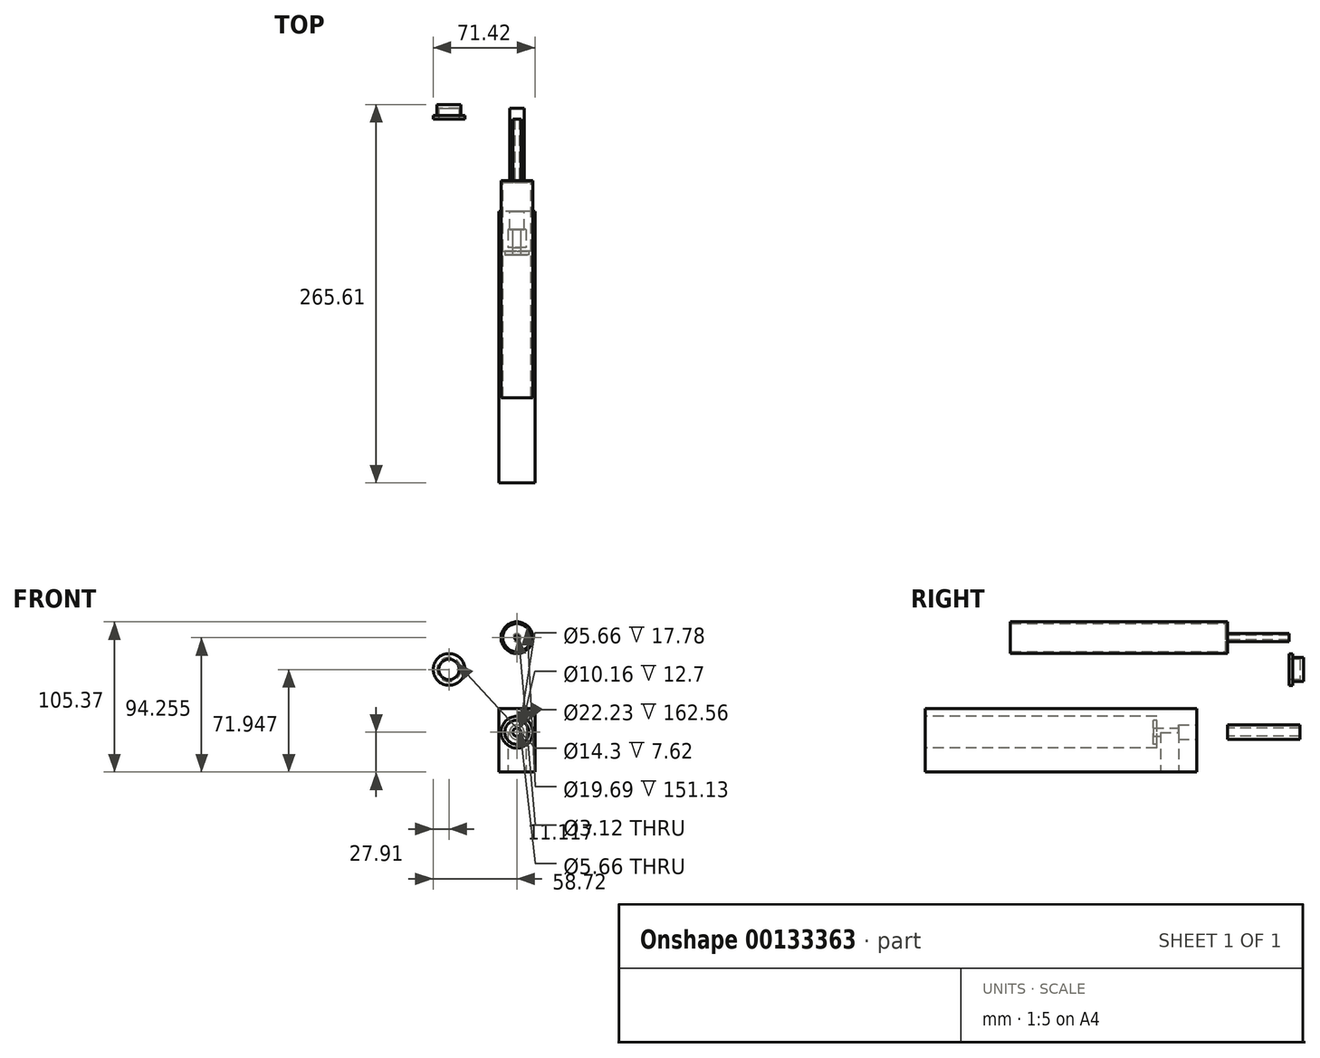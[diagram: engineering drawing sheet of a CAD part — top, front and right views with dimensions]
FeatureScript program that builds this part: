
annotation { "Feature Type Name" : "Feature", "Feature Type Description" : "" }
export const myFeature = defineFeature(function(context is Context, id is Id, definition is map)
    precondition{}
    {
        {
            var Q0;
            Q0=qCreatedBy(makeId("Right.planeOp"),FACE);
            var sketch = newSketch(context, id + "F0", { "sketchPlane" : qUnion([Q0])});
            skLineSegment(sketch, "E0.bottom", {"start": v(0, 0) * mm, "end": v(50.8, 0) * mm});
            skLineSegment(sketch, "E0.top", {"start": v(0, -2.83) * mm, "end": v(50.8, -2.83) * mm});
            skLineSegment(sketch, "E0.left", {"start": v(0, 0) * mm, "end": v(0, -2.83) * mm});
            skLineSegment(sketch, "E0.right", {"start": v(50.8, 0) * mm, "end": v(50.8, -2.83) * mm});
            skLineSegment(sketch, "E1.top", {"start": v(0, -5.08) * mm, "end": v(50.8, -5.08) * mm});
            skLineSegment(sketch, "E1.left", {"start": v(0, 0) * mm, "end": v(0, -5.08) * mm});
            skLineSegment(sketch, "E1.right", {"start": v(50.8, 0) * mm, "end": v(50.8, -5.08) * mm});
            skLineSegment(sketch, "E2.bottom", {"start": v(-21.77, 10.19) * mm, "end": v(-97.97, 10.19) * mm});
            skLineSegment(sketch, "E2.top", {"start": v(-21.77, -27.91) * mm, "end": v(-97.97, -27.91) * mm});
            skLineSegment(sketch, "E2.left", {"start": v(-21.77, 10.19) * mm, "end": v(-21.77, -27.91) * mm});
            skLineSegment(sketch, "E2.right", {"start": v(-97.97, 10.19) * mm, "end": v(-97.97, -27.91) * mm});
            skLineSegment(sketch, "E3.bottom", {"start": v(-97.97, 10.19) * mm, "end": v(-212.27, 10.19) * mm});
            skLineSegment(sketch, "E3.top", {"start": v(-97.97, -27.91) * mm, "end": v(-212.27, -27.91) * mm});
            skLineSegment(sketch, "E3.right", {"start": v(-212.27, 10.19) * mm, "end": v(-212.27, -27.91) * mm});
            skLineSegment(sketch, "E4.bottom", {"start": v(-212.27, 10.19) * mm, "end": v(-21.77, 10.19) * mm});
            skLineSegment(sketch, "E4.top", {"start": v(-212.27, 16.54) * mm, "end": v(-21.77, 16.54) * mm});
            skLineSegment(sketch, "E4.left", {"start": v(-212.27, 10.19) * mm, "end": v(-212.27, 16.54) * mm});
            skLineSegment(sketch, "E4.right", {"start": v(-21.77, 10.19) * mm, "end": v(-21.77, 16.54) * mm});
            skSolve(sketch);
        }
        {
            var Q0;
            {var subQ0=sQuery(id+"F0.wireOp",EDGE,"E0.top");Q0=makeQuery(id+"F0.imprint","IMPRINT",FACE,{"disambiguationData":[TD([[makeQuery(id+"F0.imprint","IMPRINT",EDGE,{"derivedFrom":subQ0}),-1.0]])]});}
            var Q1;
            Q1=sQuery(id+"F0.wireOp",EDGE,"E0.bottom");
            revolve(context, id + "F1", {"entities" : qUnion([Q0]), "axis" : qUnion([Q1]), "revolveType" : RevolveType.FULL});
        }
        {
            var Q0;
            Q0=makeQuery(id+"F0.imprint","IMPRINT",FACE,{"disambiguationData":[TD([[makeQuery(id+"F0.imprint","IMPRINT",EDGE,{"derivedFrom":sQuery(id+"F0.wireOp",EDGE,"E3.top")}),-1.0]])]});
            var Q1;
            Q1=makeQuery(id+"F0.imprint","IMPRINT",FACE,{"disambiguationData":[TD([[makeQuery(id+"F0.imprint","IMPRINT",EDGE,{"derivedFrom":sQuery(id+"F0.wireOp",EDGE,"E4.top")}),-1.0]])]});
            var Q2;
            Q2=makeQuery(id+"F0.imprint","IMPRINT",FACE,{"disambiguationData":[TD([[makeQuery(id+"F0.imprint","IMPRINT",EDGE,{"derivedFrom":sQuery(id+"F0.wireOp",EDGE,"E2.top")}),-1.0]])]});
            extrude(context, id + "F2", {"entities" : qUnion([Q0, Q1, Q2]), "operationType" : NewBodyOperationType.ADD, "endBound" : BoundingType.SYMMETRIC, "depth" : 25.4 * mm});
        }
        {
            var Q0;
            Q0=makeQuery(id+"F2.opExtrude","SWEPT_FACE",FACE,{"disambiguationData":[OSD([sQuery(id+"F0.wireOp",EDGE,"E2.left")])]});
            var sketch = newSketch(context, id + "F3", { "sketchPlane" : qUnion([Q0])});
            skPoint(sketch, "E5", {"position": v(0, -38.2) * mm});
            skPoint(sketch, "E5.positionSnap0", {"position": v(0, -27.91) * mm});
            skCircle(sketch, "E6", {"center": v(0, 0) * mm, "radius": 5.08 * mm});
            skCircle(sketch, "E7", {"center": v(0, 0) * mm, "radius": 2.83 * mm});
            skSolve(sketch);
        }
        {
            var Q0;
            Q0=makeQuery(id+"F3.imprint","IMPRINT",FACE,{"disambiguationData":[TD([[makeQuery(id+"F3.imprint","IMPRINT",EDGE,{"derivedFrom":sQuery(id+"F3.wireOp",EDGE,"E6")}),1.0]])]});
            extrude(context, id + "F4", {"entities" : qUnion([Q0]), "operationType" : NewBodyOperationType.REMOVE, "oppositeDirection" : true, "depth" : 12.7 * mm});
        }
        {
            var Q0;
            Q0=makeQuery(id+"F4.boolean.opBoolean","SPLIT",FACE,{"disambiguationData":[TD([makeQuery(id+"F4.opExtrude","SWEPT_FACE",FACE,{"disambiguationData":[OSD([sQuery(id+"F3.wireOp",EDGE,"E7")])]})])],"derivedFrom":makeQuery(id+"F2.opExtrude","SWEPT_FACE",FACE,{"disambiguationData":[OSD([sQuery(id+"F0.wireOp",EDGE,"E2.left")])]})});
            extrude(context, id + "F5", {"entities" : qUnion([Q0]), "operationType" : NewBodyOperationType.REMOVE, "oppositeDirection" : true, "depth" : 190.5 * mm});
        }
        {
            var Q0;
            Q0=makeQuery(id+"F2.opExtrude","SWEPT_FACE",FACE,{"disambiguationData":[OSD([sQuery(id+"F0.wireOp",EDGE,"E2.top")])]});
            var sketch = newSketch(context, id + "F6", { "sketchPlane" : qUnion([Q0])});
            skPoint(sketch, "E8", {"position": v(0, 34.47) * mm});
            skPoint(sketch, "E8.positionSnap0", {"position": v(0, 21.77) * mm});
            skPoint(sketch, "E9", {"position": v(0, 40.82) * mm});
            skLineSegment(sketch, "E10.bottom", {"start": v(6.35, 34.47) * mm, "end": v(-6.35, 34.47) * mm});
            skLineSegment(sketch, "E10.top", {"start": v(6.35, 47.17) * mm, "end": v(-6.35, 47.17) * mm});
            skLineSegment(sketch, "E10.left", {"start": v(6.35, 34.47) * mm, "end": v(6.35, 47.17) * mm});
            skLineSegment(sketch, "E10.right", {"start": v(-6.35, 34.47) * mm, "end": v(-6.35, 47.17) * mm});
            skSolve(sketch);
        }
        {
            var Q0;
            Q0=makeQuery(id+"F6.imprint","IMPRINT",FACE,{"disambiguationData":[TD([[makeQuery(id+"F6.imprint","IMPRINT",EDGE,{"derivedFrom":sQuery(id+"F6.wireOp",EDGE,"E10.bottom")}),-1.0]])]});
            extrude(context, id + "F7", {"entities" : qUnion([Q0]), "operationType" : NewBodyOperationType.REMOVE, "oppositeDirection" : true, "depth" : 27.8 * mm});
        }
        {
            var Q0;
            Q0=makeQuery(id+"F2.opExtrude","SWEPT_FACE",FACE,{"disambiguationData":[OSD([sQuery(id+"F0.wireOp",EDGE,"E3.right")])]});
            var sketch = newSketch(context, id + "F8", { "sketchPlane" : qUnion([Q0])});
            skCircle(sketch, "E11", {"center": v(0, 0) * mm, "radius": 11.11 * mm});
            skCircle(sketch, "E12", {"center": v(0, 0) * mm, "radius": 8.42 * mm});
            skSolve(sketch);
        }
        {
            var Q0;
            Q0=makeQuery(id+"F8.imprint","IMPRINT",FACE,{"disambiguationData":[TD([[makeQuery(id+"F8.imprint","IMPRINT",EDGE,{"derivedFrom":sQuery(id+"F8.wireOp",EDGE,"E11")}),1.0]])]});
            var Q1;
            Q1=makeQuery(id+"F8.imprint","IMPRINT",FACE,{"disambiguationData":[TD([[makeQuery(id+"F8.imprint","IMPRINT",EDGE,{"derivedFrom":sQuery(id+"F8.wireOp",EDGE,"E12")}),1.0]])]});
            extrude(context, id + "F9", {"entities" : qUnion([Q0, Q1]), "operationType" : NewBodyOperationType.REMOVE, "oppositeDirection" : true, "depth" : 160.02 * mm});
        }
        {
            var Q0;
            Q0=qCreatedBy(makeId("Front.planeOp"),FACE);
            var sketch = newSketch(context, id + "F10", { "sketchPlane" : qUnion([Q0])});
            skCircle(sketch, "E13", {"center": v(0, 25.97) * mm, "radius": 11.11 * mm});
            skCircle(sketch, "E14", {"center": v(0, 25.97) * mm, "radius": 2.83 * mm});
            skSolve(sketch);
        }
        {
            var Q0;
            Q0=makeQuery(id+"F10.imprint","IMPRINT",FACE,{"disambiguationData":[TD([[makeQuery(id+"F10.imprint","IMPRINT",EDGE,{"derivedFrom":sQuery(id+"F10.wireOp",EDGE,"E13")}),1.0]])]});
            var Q1;
            Q1=makeQuery(id+"F10.imprint","IMPRINT",FACE,{"disambiguationData":[TD([[makeQuery(id+"F10.imprint","IMPRINT",EDGE,{"derivedFrom":sQuery(id+"F10.wireOp",EDGE,"E14")}),1.0]])]});
            extrude(context, id + "F11", {"entities" : qUnion([Q0, Q1]), "depth" : 152.4 * mm});
        }
        {
            var Q0;
            Q0=makeQuery(id+"F10.imprint","IMPRINT",FACE,{"disambiguationData":[TD([[makeQuery(id+"F10.imprint","IMPRINT",EDGE,{"derivedFrom":sQuery(id+"F10.wireOp",EDGE,"E14")}),1.0]])]});
            extrude(context, id + "F12", {"entities" : qUnion([Q0]), "operationType" : NewBodyOperationType.ADD, "oppositeDirection" : true, "depth" : 43.18 * mm});
        }
        {
            var Q0;
            Q0=makeQuery(id+"F11.opExtrude","CAP_FACE",FACE,{"disambiguationData":[OSD([sQuery(id+"F10.wireOp",EDGE,"E13")])],"isStart":false});
            shell(context, id + "F13", {"entities" : qUnion([Q0]), "thickness" : 1.27 * mm});
        }
        {
            var Q0;
            Q0=makeQuery(id+"F12.opExtrude","CAP_FACE",FACE,{"disambiguationData":[OSD([sQuery(id+"F10.wireOp",EDGE,"E14")])],"isStart":false});
            var sketch = newSketch(context, id + "F14", { "sketchPlane" : qUnion([Q0])});
            skCircle(sketch, "E15", {"center": v(0, 25.97) * mm, "radius": 1.56 * mm});
            skCircle(sketch, "E16", {"center": v(47.6, 44.04) * mm, "radius": 11.11 * mm});
            skCircle(sketch, "E17", {"center": v(47.6, 44.04) * mm, "radius": 8.42 * mm});
            skCircle(sketch, "E18", {"center": v(47.6, 44.04) * mm, "radius": 7.15 * mm});
            skSolve(sketch);
        }
        {
            var Q0;
            Q0=makeQuery(id+"F14.imprint","IMPRINT",FACE,{"disambiguationData":[TD([[makeQuery(id+"F14.imprint","IMPRINT",EDGE,{"derivedFrom":sQuery(id+"F14.wireOp",EDGE,"E15")}),1.0]])]});
            extrude(context, id + "F15", {"entities" : qUnion([Q0]), "operationType" : NewBodyOperationType.REMOVE, "oppositeDirection" : true, "depth" : 2.54 * mm});
        }
        {
            var Q0;
            Q0=makeQuery(id+"F14.imprint","IMPRINT",FACE,{"disambiguationData":[TD([[makeQuery(id+"F14.imprint","IMPRINT",EDGE,{"derivedFrom":sQuery(id+"F14.wireOp",EDGE,"E17")}),1.0]])]});
            var Q1;
            Q1=makeQuery(id+"F14.imprint","IMPRINT",FACE,{"disambiguationData":[TD([[makeQuery(id+"F14.imprint","IMPRINT",EDGE,{"derivedFrom":sQuery(id+"F14.wireOp",EDGE,"E18")}),1.0]])]});
            extrude(context, id + "F16", {"entities" : qUnion([Q0, Q1]), "depth" : 10.16 * mm});
        }
        {
            var Q0;
            Q0=makeQuery(id+"F8.imprint","IMPRINT",FACE,{"disambiguationData":[TD([[makeQuery(id+"F8.imprint","IMPRINT",EDGE,{"derivedFrom":sQuery(id+"F8.wireOp",EDGE,"E11")}),1.0]])]});
            extrude(context, id + "F17", {"entities" : qUnion([Q0]), "operationType" : NewBodyOperationType.REMOVE, "oppositeDirection" : true, "depth" : 162.56 * mm});
        }
        {
            var Q0;
            Q0=makeQuery(id+"F14.imprint","IMPRINT",FACE,{"disambiguationData":[TD([[makeQuery(id+"F14.imprint","IMPRINT",EDGE,{"derivedFrom":sQuery(id+"F14.wireOp",EDGE,"E16")}),1.0]])]});
            extrude(context, id + "F18", {"entities" : qUnion([Q0]), "operationType" : NewBodyOperationType.ADD, "depth" : 2.54 * mm});
        }
        {
            var Q0;
            Q0=makeQuery(id+"F14.imprint","IMPRINT",FACE,{"disambiguationData":[TD([[makeQuery(id+"F14.imprint","IMPRINT",EDGE,{"derivedFrom":sQuery(id+"F14.wireOp",EDGE,"E18")}),1.0]])]});
            extrude(context, id + "F19", {"entities" : qUnion([Q0]), "operationType" : NewBodyOperationType.REMOVE, "depth" : 7.62 * mm});
        }
        {
            var Q0;
            Q0=makeQuery(id+"F11.opExtrude","SWEPT_BODY",BODY,{"disambiguationData":[OSD([sQuery(id+"F10.wireOp",EDGE,"E13")])]});
            transform(context, id + "F20", {"entities" : qUnion([Q0]), "transformType" : TransformType.TRANSLATION_3D, "dx" : 0 * mm, "dy" : 0 * mm, "dz" : 40.38 * mm, "makeCopy" : false});
        }
    });
